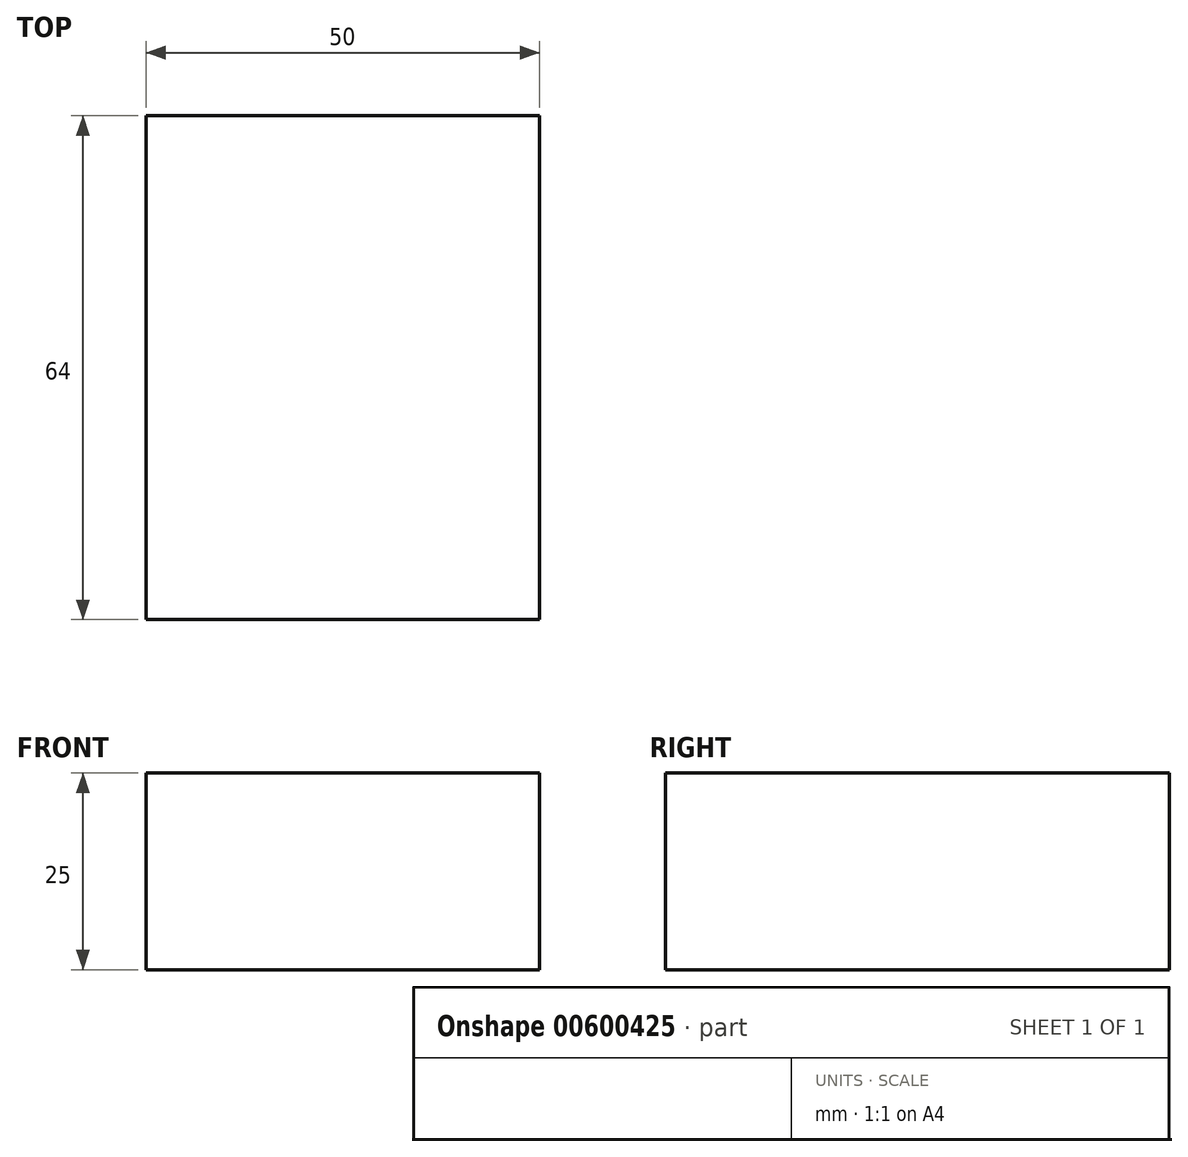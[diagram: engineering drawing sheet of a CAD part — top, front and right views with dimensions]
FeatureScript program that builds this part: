
annotation { "Feature Type Name" : "Feature", "Feature Type Description" : "" }
export const myFeature = defineFeature(function(context is Context, id is Id, definition is map)
    precondition{}
    {
        {
            var Q0;
            Q0=qCreatedBy(makeId("Top.planeOp"),FACE);
            var sketch = newSketch(context, id + "F0", { "sketchPlane" : qUnion([Q0])});
            skLineSegment(sketch, "E0.bottom", {"start": v(-112.7, -62.54) * mm, "end": v(-62.7, -62.54) * mm});
            skLineSegment(sketch, "E0.top", {"start": v(-112.7, 1.46) * mm, "end": v(-62.7, 1.46) * mm});
            skLineSegment(sketch, "E0.left", {"start": v(-112.7, -62.54) * mm, "end": v(-112.7, 1.46) * mm});
            skLineSegment(sketch, "E0.right", {"start": v(-62.7, -62.54) * mm, "end": v(-62.7, 1.46) * mm});
            skSolve(sketch);
        }
        {
            var Q0;
            Q0=makeQuery(id+"F0.imprint","IMPRINT",FACE,{"disambiguationData":[TD([[makeQuery(id+"F0.imprint","IMPRINT",EDGE,{"derivedFrom":sQuery(id+"F0.wireOp",EDGE,"E0.bottom")}),1.0]])]});
            extrude(context, id + "F1", {"entities" : qUnion([Q0]), "depth" : 25 * mm, "offsetDistance" : 25 * mm});
        }
    });
